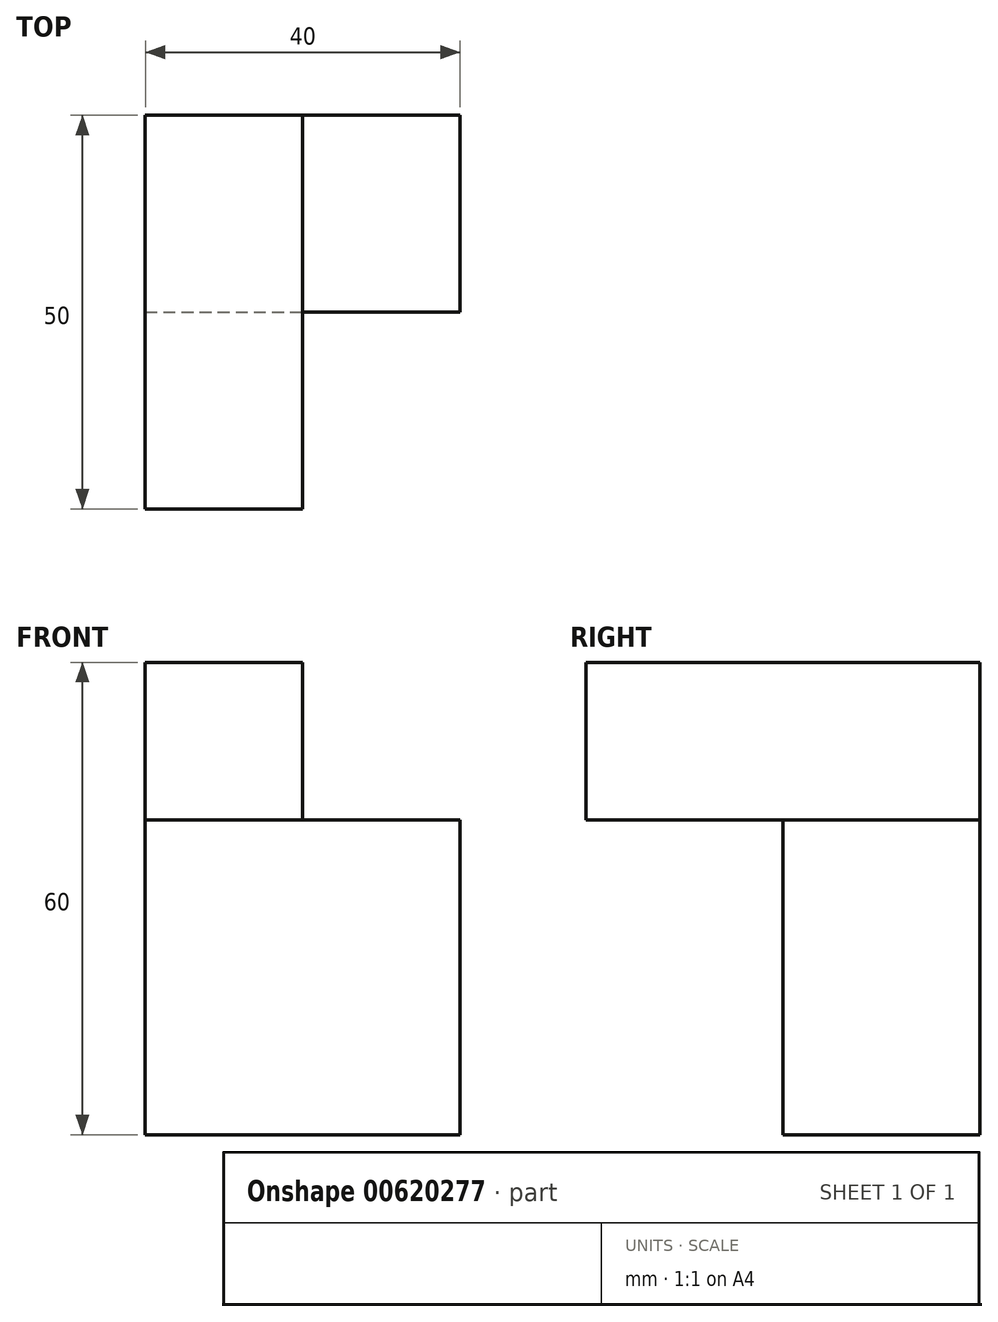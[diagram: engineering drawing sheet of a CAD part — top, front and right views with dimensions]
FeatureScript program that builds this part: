
annotation { "Feature Type Name" : "Feature", "Feature Type Description" : "" }
export const myFeature = defineFeature(function(context is Context, id is Id, definition is map)
    precondition{}
    {
        {
            var Q0;
            Q0=qCreatedBy(makeId("Front.planeOp"),FACE);
            var sketch = newSketch(context, id + "F0", { "sketchPlane" : qUnion([Q0])});
            skLineSegment(sketch, "E0", {"start": v(-25.83, 38.95) * mm, "end": v(-25.83, -21.05) * mm});
            skLineSegment(sketch, "E1", {"start": v(-25.83, -21.05) * mm, "end": v(14.17, -21.05) * mm});
            skLineSegment(sketch, "E2", {"start": v(14.17, -21.05) * mm, "end": v(14.17, 18.95) * mm});
            skLineSegment(sketch, "E3", {"start": v(14.17, 18.95) * mm, "end": v(-5.83, 18.95) * mm});
            skLineSegment(sketch, "E4", {"start": v(-5.83, 18.95) * mm, "end": v(-5.83, 38.95) * mm});
            skLineSegment(sketch, "E5", {"start": v(-5.83, 38.95) * mm, "end": v(-25.83, 38.95) * mm});
            skSolve(sketch);
        }
        {
            var Q0;
            Q0=makeQuery(id+"F0.imprint","IMPRINT",FACE,{"disambiguationData":[TD([[makeQuery(id+"F0.imprint","IMPRINT",EDGE,{"derivedFrom":sQuery(id+"F0.wireOp",EDGE,"E0")}),1.0]])]});
            extrude(context, id + "F1", {"entities" : qUnion([Q0]), "depth" : 25 * mm, "offsetDistance" : 25 * mm});
        }
        {
            var Q0;
            Q0=makeQuery(id+"F1.opExtrude","CAP_FACE",FACE,{"disambiguationData":[OSD([sQuery(id+"F0.wireOp",EDGE,"E0"),sQuery(id+"F0.wireOp",EDGE,"E1"),sQuery(id+"F0.wireOp",EDGE,"E2"),sQuery(id+"F0.wireOp",EDGE,"E3"),sQuery(id+"F0.wireOp",EDGE,"E4"),sQuery(id+"F0.wireOp",EDGE,"E5")])],"isStart":false});
            var sketch = newSketch(context, id + "F2", { "sketchPlane" : qUnion([Q0])});
            skLineSegment(sketch, "E6.bottom", {"start": v(-25.83, 38.95) * mm, "end": v(-5.83, 38.95) * mm});
            skLineSegment(sketch, "E6.top", {"start": v(-25.83, 18.95) * mm, "end": v(-5.83, 18.95) * mm});
            skLineSegment(sketch, "E6.left", {"start": v(-25.83, 38.95) * mm, "end": v(-25.83, 18.95) * mm});
            skLineSegment(sketch, "E6.right", {"start": v(-5.83, 38.95) * mm, "end": v(-5.83, 18.95) * mm});
            skSolve(sketch);
        }
        {
            var Q0;
            Q0=makeQuery(id+"F2.imprint","IMPRINT",FACE,{"disambiguationData":[TD([[makeQuery(id+"F2.imprint","IMPRINT",EDGE,{"derivedFrom":sQuery(id+"F2.wireOp",EDGE,"E6.bottom")}),1.0]])]});
            extrude(context, id + "F3", {"entities" : qUnion([Q0]), "operationType" : NewBodyOperationType.ADD, "depth" : 25 * mm, "offsetDistance" : 25 * mm});
        }
    });
